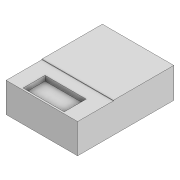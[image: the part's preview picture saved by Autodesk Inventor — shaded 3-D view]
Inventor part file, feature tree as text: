
AUTODESK INVENTOR PART (.ipt)
format: ipt  version: 2022 (Build 260153000, 153)  size: 121,344 bytes
history: native  units: mm
features: extrude x4, sketch x4, projected_geometry x3
ambient origin geometry x8: Origin, YZ Plane, XZ Plane, XY Plane, X Axis, Y Axis, Z Axis, Center Point
bodies: Volumenkörper1 (feature_tree)
feature tree (11):
  extrude  "Extrusion1"  Depth=17.5mm
  extrude  "Extrusion2"  Depth=7.5mm
  extrude  "Extrusion3"  Depth=1.0mm TaperAngle=0.0deg
  extrude  "Extrusion4"  Depth=0.1mm TaperAngle=0.0deg
  sketch  "Skizze1"  dims[d0=13.0mm d1=17.5mm]
  sketch  "Skizze2"  dims[d2=5.5mm d3=0.0mm d4=7.5mm]
  projected_geometry  "Projizierte Kontur1"
  sketch  "Skizze3"  dims[d5=4.0mm d6=1.0mm d7=0.0mm]
  projected_geometry  "Projizierte Kontur2"
  sketch  "Skizze4"  dims[d8=6.5mm d9=0.1mm d10=0.0mm d11=7.3mm d12=4.0mm d13=0.1mm d14=0.0mm]
  projected_geometry  "Projizierte Kontur3"
